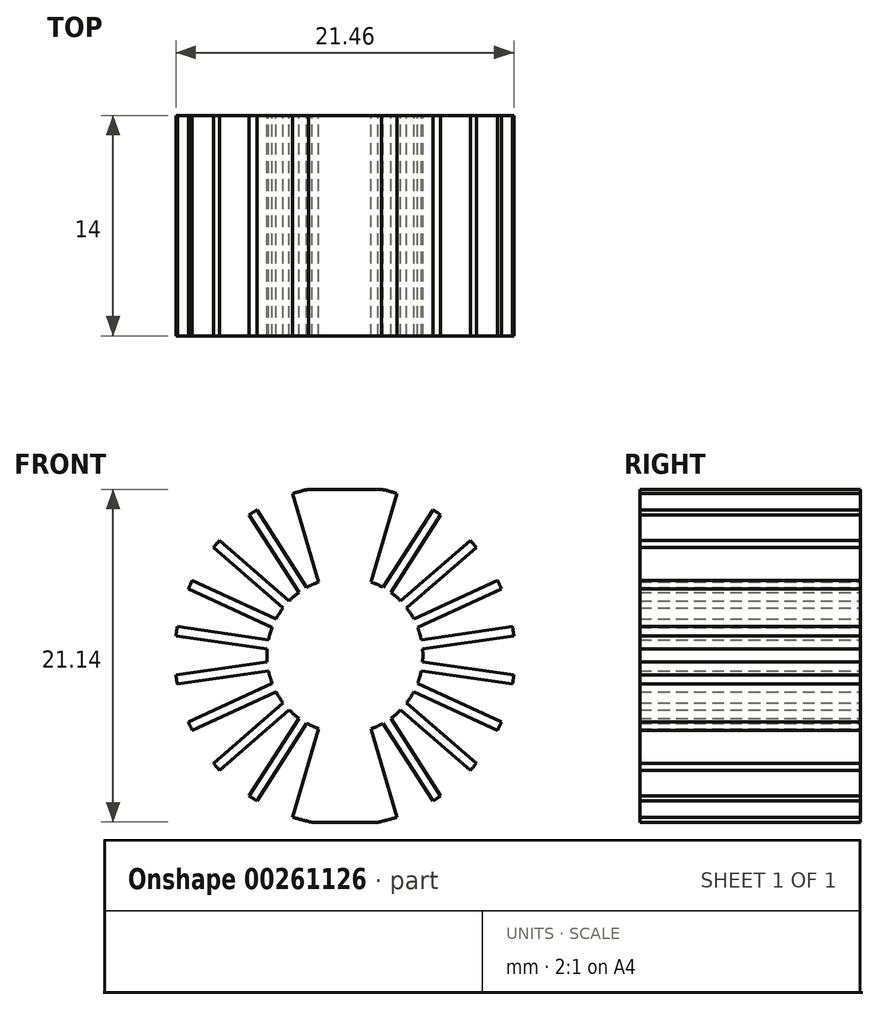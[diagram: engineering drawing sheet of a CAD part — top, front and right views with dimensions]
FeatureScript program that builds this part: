
annotation { "Feature Type Name" : "Feature", "Feature Type Description" : "" }
export const myFeature = defineFeature(function(context is Context, id is Id, definition is map)
    precondition{}
    {
        {
            var Q0;
            Q0=qCreatedBy(makeId("Front.planeOp"),FACE);
            var sketch = newSketch(context, id + "F0", { "sketchPlane" : qUnion([Q0])});
            skArc(sketch, "E0", {"start": v(-5.6, 9.24) * mm, "mid": v(-5.84, 9.09) * mm, "end": v(-6.08, 8.92) * mm});
            skArc(sketch, "E1", {"start": v(-1.67, 4.66) * mm, "mid": v(-2.06, 4.5) * mm, "end": v(-2.43, 4.31) * mm});
            skLineSegment(sketch, "E2.1.0", {"start": v(-3.32, 10.28) * mm, "end": v(-1.67, 4.66) * mm});
            skLineSegment(sketch, "E2.2.0", {"start": v(-6.08, 8.92) * mm, "end": v(-2.92, 4) * mm});
            skLineSegment(sketch, "E2.2.1", {"start": v(-5.6, 9.24) * mm, "end": v(-2.43, 4.31) * mm});
            skLineSegment(sketch, "E2.3.0", {"start": v(-8.35, 6.85) * mm, "end": v(-3.93, 3.02) * mm});
            skLineSegment(sketch, "E2.3.1", {"start": v(-7.97, 7.3) * mm, "end": v(-3.54, 3.46) * mm});
            skLineSegment(sketch, "E2.4.0", {"start": v(-9.94, 4.22) * mm, "end": v(-4.62, 1.79) * mm});
            skLineSegment(sketch, "E2.4.1", {"start": v(-9.7, 4.75) * mm, "end": v(-4.37, 2.32) * mm});
            skLineSegment(sketch, "E2.5.0", {"start": v(-10.73, 1.25) * mm, "end": v(-4.93, 0.41) * mm});
            skLineSegment(sketch, "E2.5.1", {"start": v(-10.64, 1.83) * mm, "end": v(-4.85, 1) * mm});
            skLineSegment(sketch, "E2.6.0", {"start": v(-10.64, -1.83) * mm, "end": v(-4.85, -1) * mm});
            skLineSegment(sketch, "E2.6.1", {"start": v(-10.73, -1.25) * mm, "end": v(-4.93, -0.41) * mm});
            skLineSegment(sketch, "E2.7.0", {"start": v(-9.7, -4.75) * mm, "end": v(-4.37, -2.32) * mm});
            skLineSegment(sketch, "E2.7.1", {"start": v(-9.94, -4.22) * mm, "end": v(-4.62, -1.79) * mm});
            skLineSegment(sketch, "E2.8.0", {"start": v(-7.97, -7.3) * mm, "end": v(-3.54, -3.46) * mm});
            skLineSegment(sketch, "E2.8.1", {"start": v(-8.35, -6.85) * mm, "end": v(-3.93, -3.02) * mm});
            skLineSegment(sketch, "E2.9.0", {"start": v(-5.6, -9.24) * mm, "end": v(-2.43, -4.31) * mm});
            skLineSegment(sketch, "E2.9.1", {"start": v(-6.08, -8.92) * mm, "end": v(-2.92, -4) * mm});
            skLineSegment(sketch, "E2.10.1", {"start": v(-3.32, -10.28) * mm, "end": v(-1.67, -4.66) * mm});
            skLineSegment(sketch, "E2.12.0", {"start": v(3.32, -10.28) * mm, "end": v(1.67, -4.66) * mm});
            skLineSegment(sketch, "E2.13.0", {"start": v(6.08, -8.92) * mm, "end": v(2.92, -4) * mm});
            skLineSegment(sketch, "E2.13.1", {"start": v(5.6, -9.24) * mm, "end": v(2.43, -4.31) * mm});
            skLineSegment(sketch, "E2.14.0", {"start": v(8.35, -6.85) * mm, "end": v(3.93, -3.02) * mm});
            skLineSegment(sketch, "E2.14.1", {"start": v(7.97, -7.3) * mm, "end": v(3.54, -3.46) * mm});
            skLineSegment(sketch, "E2.15.0", {"start": v(9.94, -4.22) * mm, "end": v(4.62, -1.79) * mm});
            skLineSegment(sketch, "E2.15.1", {"start": v(9.7, -4.75) * mm, "end": v(4.37, -2.32) * mm});
            skLineSegment(sketch, "E2.16.0", {"start": v(10.73, -1.25) * mm, "end": v(4.93, -0.41) * mm});
            skLineSegment(sketch, "E2.16.1", {"start": v(10.64, -1.83) * mm, "end": v(4.85, -1) * mm});
            skLineSegment(sketch, "E2.17.0", {"start": v(10.64, 1.83) * mm, "end": v(4.85, 1) * mm});
            skLineSegment(sketch, "E2.17.1", {"start": v(10.73, 1.25) * mm, "end": v(4.93, 0.41) * mm});
            skLineSegment(sketch, "E2.18.0", {"start": v(9.7, 4.75) * mm, "end": v(4.37, 2.32) * mm});
            skLineSegment(sketch, "E2.18.1", {"start": v(9.94, 4.22) * mm, "end": v(4.62, 1.79) * mm});
            skLineSegment(sketch, "E2.19.0", {"start": v(7.97, 7.3) * mm, "end": v(3.54, 3.46) * mm});
            skLineSegment(sketch, "E2.19.1", {"start": v(8.35, 6.85) * mm, "end": v(3.93, 3.02) * mm});
            skLineSegment(sketch, "E2.20.0", {"start": v(5.6, 9.24) * mm, "end": v(2.43, 4.31) * mm});
            skLineSegment(sketch, "E2.20.1", {"start": v(6.08, 8.92) * mm, "end": v(2.92, 4) * mm});
            skLineSegment(sketch, "E2.21.1", {"start": v(3.32, 10.28) * mm, "end": v(1.67, 4.66) * mm});
            skArc(sketch, "E3.trimOffspring", {"start": v(3.32, 10.28) * mm, "mid": v(2.82, 10.43) * mm, "end": v(2.31, 10.55) * mm});
            skArc(sketch, "E4.trimOffspring", {"start": v(-3.32, -10.28) * mm, "mid": v(-2.72, -10.45) * mm, "end": v(-2.1, -10.6) * mm});
            skArc(sketch, "E5.trimOffspring", {"start": v(5.6, -9.24) * mm, "mid": v(5.84, -9.09) * mm, "end": v(6.08, -8.92) * mm});
            skArc(sketch, "E6.trimOffspring", {"start": v(7.97, -7.3) * mm, "mid": v(8.16, -7.07) * mm, "end": v(8.35, -6.85) * mm});
            skArc(sketch, "E7.trimOffspring", {"start": v(9.7, -4.75) * mm, "mid": v(9.82, -4.49) * mm, "end": v(9.94, -4.22) * mm});
            skArc(sketch, "E8.trimOffspring", {"start": v(10.64, -1.83) * mm, "mid": v(10.7, -1.54) * mm, "end": v(10.73, -1.25) * mm});
            skArc(sketch, "E9.trimOffspring", {"start": v(10.73, 1.25) * mm, "mid": v(10.7, 1.54) * mm, "end": v(10.64, 1.83) * mm});
            skArc(sketch, "E10.trimOffspring", {"start": v(9.94, 4.22) * mm, "mid": v(9.82, 4.49) * mm, "end": v(9.7, 4.75) * mm});
            skArc(sketch, "E11.trimOffspring", {"start": v(8.35, 6.85) * mm, "mid": v(8.16, 7.07) * mm, "end": v(7.97, 7.3) * mm});
            skArc(sketch, "E12.trimOffspring", {"start": v(6.08, 8.92) * mm, "mid": v(5.84, 9.09) * mm, "end": v(5.6, 9.24) * mm});
            skArc(sketch, "E13.trimOffspring", {"start": v(-7.97, 7.3) * mm, "mid": v(-8.16, 7.07) * mm, "end": v(-8.35, 6.85) * mm});
            skArc(sketch, "E14.trimOffspring", {"start": v(-9.7, 4.75) * mm, "mid": v(-9.82, 4.49) * mm, "end": v(-9.94, 4.22) * mm});
            skArc(sketch, "E15.trimOffspring", {"start": v(-10.64, 1.83) * mm, "mid": v(-10.7, 1.54) * mm, "end": v(-10.73, 1.25) * mm});
            skArc(sketch, "E16.trimOffspring", {"start": v(-10.73, -1.25) * mm, "mid": v(-10.7, -1.54) * mm, "end": v(-10.64, -1.83) * mm});
            skArc(sketch, "E17.trimOffspring", {"start": v(-9.94, -4.22) * mm, "mid": v(-9.82, -4.49) * mm, "end": v(-9.7, -4.75) * mm});
            skArc(sketch, "E18.trimOffspring", {"start": v(-8.35, -6.85) * mm, "mid": v(-8.16, -7.07) * mm, "end": v(-7.97, -7.3) * mm});
            skArc(sketch, "E19.trimOffspring", {"start": v(-6.08, -8.92) * mm, "mid": v(-5.84, -9.09) * mm, "end": v(-5.6, -9.24) * mm});
            skArc(sketch, "E20.trimOffspring", {"start": v(-2.92, 4) * mm, "mid": v(-3.24, 3.74) * mm, "end": v(-3.54, 3.46) * mm});
            skArc(sketch, "E21.trimOffspring", {"start": v(-3.93, 3.02) * mm, "mid": v(-4.16, 2.68) * mm, "end": v(-4.37, 2.32) * mm});
            skArc(sketch, "E22.trimOffspring", {"start": v(-4.62, 1.79) * mm, "mid": v(-4.75, 1.4) * mm, "end": v(-4.85, 1) * mm});
            skArc(sketch, "E23.trimOffspring", {"start": v(-4.93, 0.41) * mm, "mid": v(-4.95, 0) * mm, "end": v(-4.93, -0.41) * mm});
            skArc(sketch, "E24.trimOffspring", {"start": v(-4.85, -1) * mm, "mid": v(-4.75, -1.4) * mm, "end": v(-4.62, -1.79) * mm});
            skArc(sketch, "E25.trimOffspring", {"start": v(-4.37, -2.32) * mm, "mid": v(-4.16, -2.68) * mm, "end": v(-3.93, -3.02) * mm});
            skArc(sketch, "E26.trimOffspring", {"start": v(-3.54, -3.46) * mm, "mid": v(-3.24, -3.74) * mm, "end": v(-2.92, -4) * mm});
            skArc(sketch, "E27.trimOffspring", {"start": v(-2.43, -4.31) * mm, "mid": v(-2.06, -4.5) * mm, "end": v(-1.67, -4.66) * mm});
            skArc(sketch, "E28.trimOffspring", {"start": v(1.67, -4.66) * mm, "mid": v(2.06, -4.5) * mm, "end": v(2.43, -4.31) * mm});
            skArc(sketch, "E29.trimOffspring", {"start": v(2.92, -4) * mm, "mid": v(3.24, -3.74) * mm, "end": v(3.54, -3.46) * mm});
            skArc(sketch, "E30.trimOffspring", {"start": v(3.93, -3.02) * mm, "mid": v(4.16, -2.68) * mm, "end": v(4.37, -2.32) * mm});
            skArc(sketch, "E31.trimOffspring", {"start": v(4.62, -1.79) * mm, "mid": v(4.75, -1.4) * mm, "end": v(4.85, -1) * mm});
            skArc(sketch, "E32.trimOffspring", {"start": v(4.93, -0.41) * mm, "mid": v(4.95, 0) * mm, "end": v(4.93, 0.41) * mm});
            skArc(sketch, "E33.trimOffspring", {"start": v(4.85, 1) * mm, "mid": v(4.75, 1.4) * mm, "end": v(4.62, 1.79) * mm});
            skArc(sketch, "E34.trimOffspring", {"start": v(4.37, 2.32) * mm, "mid": v(4.16, 2.68) * mm, "end": v(3.93, 3.02) * mm});
            skArc(sketch, "E35.trimOffspring", {"start": v(3.54, 3.46) * mm, "mid": v(3.24, 3.74) * mm, "end": v(2.92, 4) * mm});
            skArc(sketch, "E36.trimOffspring", {"start": v(2.43, 4.31) * mm, "mid": v(2.06, 4.5) * mm, "end": v(1.67, 4.66) * mm});
            skLineSegment(sketch, "E37", {"start": v(0, 0) * mm, "end": v(0, 10.55) * mm});
            skLineSegment(sketch, "E38", {"start": v(0, 0) * mm, "end": v(0, -10.55) * mm});
            skPoint(sketch, "E38.endSnap0", {"position": v(0, -10.8) * mm});
            skLineSegment(sketch, "E39", {"start": v(-2.1, -10.6) * mm, "end": v(2.1, -10.6) * mm});
            skArc(sketch, "E40.trimOffspring", {"start": v(2.1, -10.6) * mm, "mid": v(2.72, -10.45) * mm, "end": v(3.32, -10.28) * mm});
            skLineSegment(sketch, "E41", {"start": v(-2.31, 10.55) * mm, "end": v(2.31, 10.55) * mm});
            skArc(sketch, "E42.trimOffspring", {"start": v(-2.31, 10.55) * mm, "mid": v(-2.82, 10.43) * mm, "end": v(-3.32, 10.28) * mm});
            skSolve(sketch);
        }
        {
            var Q0;
            Q0=qSketchRegion(id+"F0",true);
            extrude(context, id + "F1", {"entities" : qUnion([Q0]), "depth" : 14 * mm});
        }
    });
